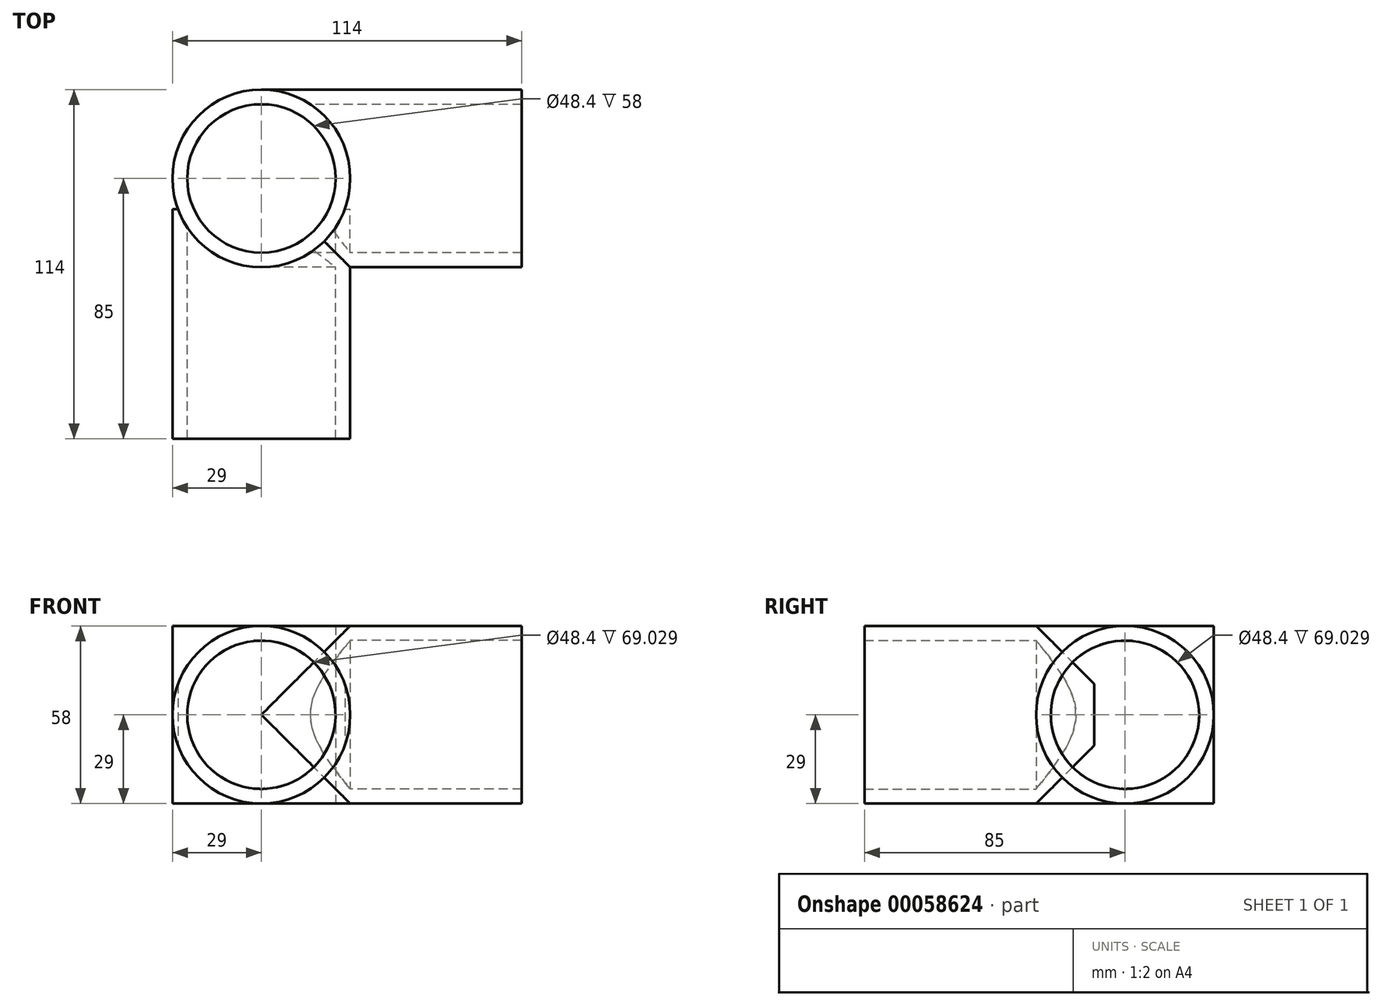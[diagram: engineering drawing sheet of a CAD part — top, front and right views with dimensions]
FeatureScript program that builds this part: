
annotation { "Feature Type Name" : "Feature", "Feature Type Description" : "" }
export const myFeature = defineFeature(function(context is Context, id is Id, definition is map)
    precondition{}
    {
        {
            var Q0;
            Q0=qCreatedBy(makeId("Front.planeOp"),FACE);
            var sketch = newSketch(context, id + "F0", { "sketchPlane" : qUnion([Q0])});
            skCircle(sketch, "E0", {"center": v(0, 0) * mm, "radius": 29 * mm});
            skCircle(sketch, "E1", {"center": v(0, 0) * mm, "radius": 24.2 * mm});
            skSolve(sketch);
        }
        {
            var Q0;
            Q0=makeQuery(id+"F0.imprint","IMPRINT",FACE,{"disambiguationData":[TD([[makeQuery(id+"F0.imprint","IMPRINT",EDGE,{"derivedFrom":sQuery(id+"F0.wireOp",EDGE,"E0")}),1.0]])]});
            extrude(context, id + "F1", {"entities" : qUnion([Q0]), "depth" : 75 * mm});
        }
        {
            var Q0;
            Q0=qCreatedBy(makeId("Top.planeOp"),FACE);
            var sketch = newSketch(context, id + "F2", { "sketchPlane" : qUnion([Q0])});
            skCircle(sketch, "E2", {"center": v(0, 10) * mm, "radius": 24.2 * mm});
            skCircle(sketch, "E3", {"center": v(0, 10) * mm, "radius": 29 * mm});
            skSolve(sketch);
        }
        {
            var Q0;
            Q0=qSketchRegion(id+"F2",true);
            extrude(context, id + "F3", {"entities" : qUnion([Q0]), "operationType" : NewBodyOperationType.ADD, "depth" : 29 * mm, "hasSecondDirection" : true, "secondDirectionOppositeDirection" : true, "secondDirectionDepth" : 29 * mm});
        }
        {
            var Q0;
            Q0=makeQuery(id+"F3.opExtrude","CAP_FACE",FACE,{"disambiguationData":[OSD([sQuery(id+"F2.wireOp",EDGE,"E2"),sQuery(id+"F2.wireOp",EDGE,"E3")])],"isStart":false});
            var sketch = newSketch(context, id + "F4", { "sketchPlane" : qUnion([Q0])});
            skCircle(sketch, "E4", {"center": v(0, 10) * mm, "radius": 24.2 * mm});
            skSolve(sketch);
        }
        {
            var Q0;
            Q0=qSketchRegion(id+"F4",true);
            extrude(context, id + "F5", {"entities" : qUnion([Q0]), "operationType" : NewBodyOperationType.REMOVE, "endBound" : BoundingType.THROUGH_ALL, "oppositeDirection" : true, "depth" : 25 * mm});
        }
        {
            var Q0;
            Q0=qCreatedBy(makeId("Right.planeOp"),FACE);
            var sketch = newSketch(context, id + "F6", { "sketchPlane" : qUnion([Q0])});
            skCircle(sketch, "E5", {"center": v(10, 0) * mm, "radius": 29 * mm});
            skCircle(sketch, "E6", {"center": v(10, 0) * mm, "radius": 24.2 * mm});
            skSolve(sketch);
        }
        {
            var Q0;
            Q0 = qSketchRegion(id + "F6", true);
            extrude(context, id + "F7", {"entities" : qUnion([Q0]), "operationType" : NewBodyOperationType.ADD, "depth" : 85 * mm});
        }
        {
            var Q0;
            Q0=makeQuery(id+"F3.opExtrude","CAP_FACE",FACE,{"disambiguationData":[OSD([sQuery(id+"F2.wireOp",EDGE,"E2"),sQuery(id+"F2.wireOp",EDGE,"E3")])],"isStart":false});
            var sketch = newSketch(context, id + "F8", { "sketchPlane" : qUnion([Q0])});
            skCircle(sketch, "E7", {"center": v(0, 10) * mm, "radius": 24.2 * mm});
            skSolve(sketch);
        }
        {
            var Q0;
            Q0 = qSketchRegion(id + "F8", true);
            extrude(context, id + "F9", {"entities" : qUnion([Q0]), "operationType" : NewBodyOperationType.REMOVE, "endBound" : BoundingType.THROUGH_ALL, "oppositeDirection" : true, "depth" : 25 * mm});
        }
    });
